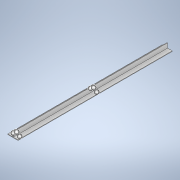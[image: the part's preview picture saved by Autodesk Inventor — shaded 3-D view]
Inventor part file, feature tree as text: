
AUTODESK INVENTOR PART (.ipt)
format: ipt  version: 2020.2 (Build 242310000, 310)  size: 157,696 bytes
history: native  units: in
note: dims shown in document units (in); Inventor stores cm internally (conversion verified against a paired STEP export)
features: sketch x3, hole x2, extrude x1
ambient origin geometry x8: Origin, YZ Plane, XZ Plane, XY Plane, X Axis, Y Axis, Z Axis, Center Point
bodies: Solid1 (feature_tree)
feature tree (6):
  extrude  "Extrusion1"  Depth=1.1811in
  hole  "Hole1"  [1 undecoded]
  hole  "Hole2"  [1 undecoded]
  sketch  "Sketch1"  dims[d0=0.1181in d2=1.1811in]
  sketch  "Sketch2"  dims[d5=0.1181in d6=35.4331in d7=0.0in]
  sketch  "Sketch3"  dims[d8=0.5906in d9=0.5906in d10=0.5906in d11=0.5906in d12=17.7165in d13=17.7165in d14=0.5906in d15=0.5906in d16=17.7165in d17=17.7165in d18=0.5906in d19=0.5906in d20=17.7165in d21=17.7165in d22=0.5906in d23=0.5906in d24=0.15in d25=0.2953in d26=0.1476in d27=0.0984in d28=90.0deg d29=0.3937in d30=0.8108in d31=0.5906in d32=0.5906in d33=17.7165in d34=0.5906in d35=17.7165in d36=17.7165in d37=0.5906in d38=0.5906in d39=0.15in d40=0.2953in d41=0.1476in d42=0.0984in d43=90.0deg d44=0.3937in d45=0.8108in d50=0.0in d51=0.0in d52=0.0in d53=0.0in d58=0.0in d59=0.0in d60=0.0in d61=0.0in]
note: 2 required parameter values undecoded (feature->parameter linkage not recoverable at this tier; creation-order binding heuristic only, values carry confidence <= 0.55)
